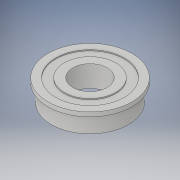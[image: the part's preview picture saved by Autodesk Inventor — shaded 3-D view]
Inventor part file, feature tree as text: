
AUTODESK INVENTOR PART (.ipt)
format: ipt  version: 2017 (Build 210142000, 142)  size: 126,976 bytes
history: native  units: in
note: dims shown in document units (in); Inventor stores cm internally (conversion verified against a paired STEP export)
features: revolve x1
ambient origin geometry x8: Origin, YZ Plane, XZ Plane, XY Plane, X Axis, Y Axis, Z Axis, Center Point
bodies: Solid1 (feature_tree)
feature tree (1):
  revolve  "Revolve1"  [1 undecoded]
note: 1 required parameter value undecoded (feature->parameter linkage not recoverable at this tier; creation-order binding heuristic only, values carry confidence <= 0.55)
